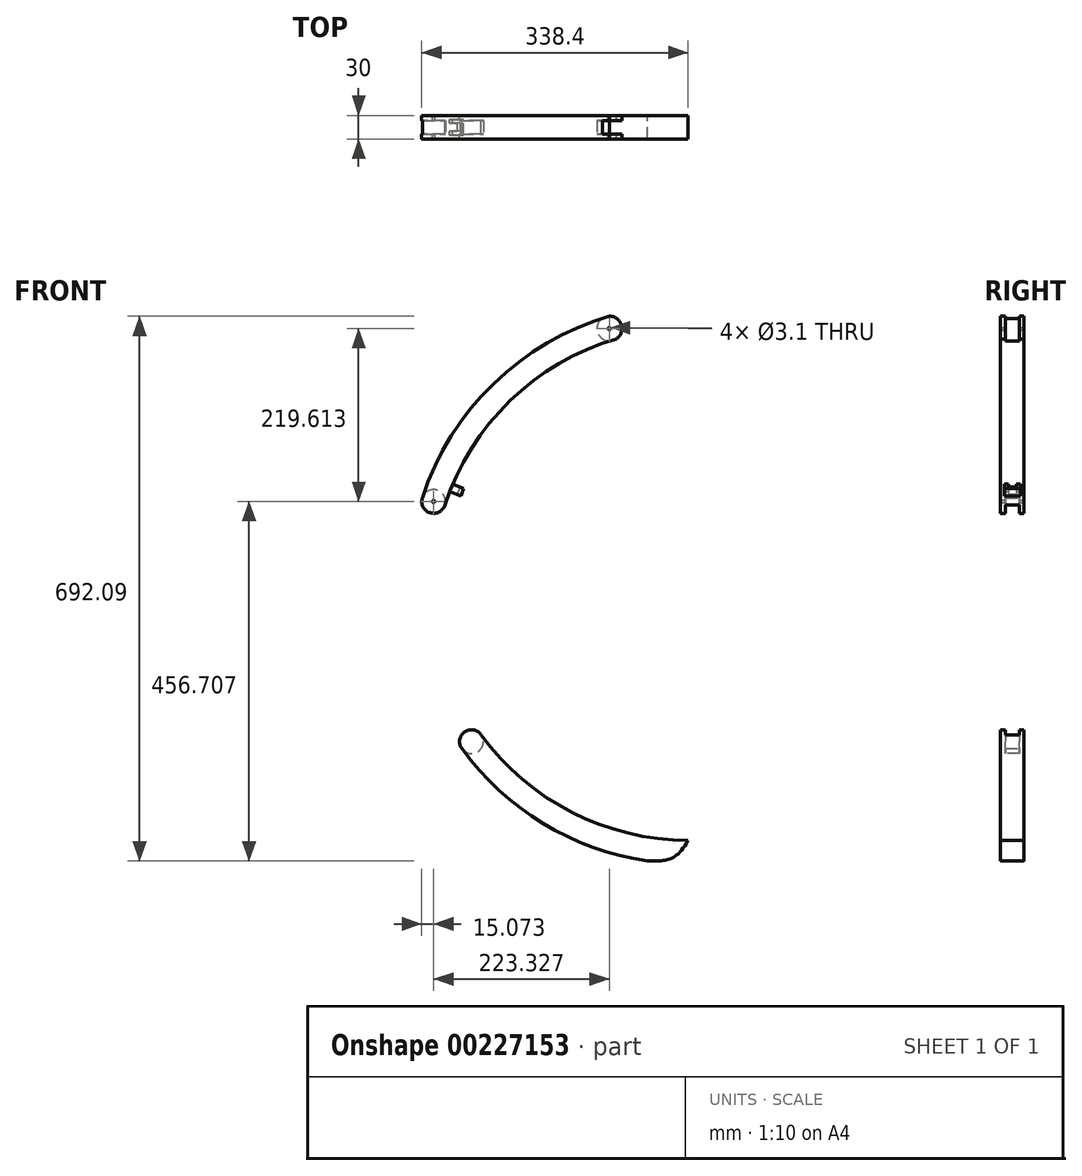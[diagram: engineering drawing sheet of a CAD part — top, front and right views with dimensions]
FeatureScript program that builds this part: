
annotation { "Feature Type Name" : "Feature", "Feature Type Description" : "" }
export const myFeature = defineFeature(function(context is Context, id is Id, definition is map)
    precondition{}
    {
        {
            var Q0;
            Q0=qCreatedBy(makeId("Front.planeOp"),FACE);
            var sketch = newSketch(context, id + "F0", { "sketchPlane" : qUnion([Q0])});
            skLineSegment(sketch, "E0.bottom", {"start": v(-100, 309.23) * mm, "end": v(100, 309.23) * mm});
            skLineSegment(sketch, "E0.top", {"start": v(-100, 340.77) * mm, "end": v(100, 340.77) * mm});
            skLineSegment(sketch, "E0.left", {"start": v(-100, 309.23) * mm, "end": v(-100, 340.77) * mm, "construction": true});
            skLineSegment(sketch, "E0.right", {"start": v(100, 309.23) * mm, "end": v(100, 340.77) * mm});
            skPoint(sketch, "E0.middle", {"position": v(0, 325) * mm});
            skArc(sketch, "E1", {"start": v(-100, 309.23) * mm, "mid": v(-229.54, 230.08) * mm, "end": v(-309, 100.72) * mm});
            skArc(sketch, "E2", {"start": v(-309, 100.72) * mm, "mid": v(-321.03, -50.62) * mm, "end": v(-263.02, -190.9) * mm});
            skArc(sketch, "E3", {"start": v(-263.02, -190.9) * mm, "mid": v(-147.61, -289.54) * mm, "end": v(0, -325) * mm});
            skArc(sketch, "E4", {"start": v(0, -325) * mm, "mid": v(321.03, 50.62) * mm, "end": v(-100, 309.23) * mm});
            skLineSegment(sketch, "E5", {"start": v(0, -325) * mm, "end": v(0, 0) * mm});
            skLineSegment(sketch, "E6", {"start": v(-100, 309.23) * mm, "end": v(-309, 100.72) * mm, "construction": true});
            skLineSegment(sketch, "E7", {"start": v(-263.02, -190.9) * mm, "end": v(-309, 100.72) * mm, "construction": true});
            skLineSegment(sketch, "E8", {"start": v(0, -325) * mm, "end": v(-263.02, -190.9) * mm, "construction": true});
            skCircle(sketch, "E9", {"center": v(-100, 325) * mm, "radius": 15.77 * mm});
            skCircle(sketch, "E10", {"center": v(-100, 325) * mm, "radius": 1.55 * mm});
            skCircle(sketch, "E11", {"center": v(0, 0) * mm, "radius": 355.14 * mm});
            skLineSegment(sketch, "E12", {"start": v(0, 0) * mm, "end": v(-309, 100.72) * mm, "construction": true});
            skLineSegment(sketch, "E13", {"start": v(-309, 100.72) * mm, "end": v(-337.65, 110.06) * mm, "construction": true});
            skCircle(sketch, "E14", {"center": v(-323.33, 105.39) * mm, "radius": 15.07 * mm});
            skCircle(sketch, "E15", {"center": v(-323.33, 105.39) * mm, "radius": 1.55 * mm});
            skLineSegment(sketch, "E16", {"start": v(0, 0) * mm, "end": v(-263.02, -190.9) * mm, "construction": true});
            skLineSegment(sketch, "E17", {"start": v(-263.02, -190.9) * mm, "end": v(-287.4, -208.61) * mm, "construction": true});
            skLineSegment(sketch, "E18", {"start": v(0, -325) * mm, "end": v(0, -355.14) * mm, "construction": true});
            skCircle(sketch, "E19", {"center": v(-275.21, -199.76) * mm, "radius": 15.07 * mm});
            skFitSpline(sketch, "E20", {"points": [v(0, -325) * mm, v(-51.95, -351.32) * mm], "startDerivative": vector(-47.92, -89.33) * mm, "endDerivative": vector(-61.3, -2.04) * mm});
            skLineSegment(sketch, "E21", {"start": v(-330.86, 129.04) * mm, "end": v(0, 0) * mm, "construction": true});
            skLineSegment(sketch, "E22", {"start": v(0, 0) * mm, "end": v(-350.8, -55.31) * mm, "construction": true});
            skLineSegment(sketch, "E23", {"start": v(-302.79, 118.1) * mm, "end": v(-284.01, 110.77) * mm});
            skLineSegment(sketch, "E24", {"start": v(-284.01, 110.77) * mm, "end": v(-280.38, 120.08) * mm});
            skLineSegment(sketch, "E25", {"start": v(-280.38, 120.08) * mm, "end": v(-299, 127.35) * mm});
            skLineSegment(sketch, "E26", {"start": v(-289.7, 123.72) * mm, "end": v(-293.33, 114.4) * mm});
            skLineSegment(sketch, "E27.MirrorCS", {"start": v(-294.73, 77.87) * mm, "end": v(-297.29, 68.2) * mm});
            skLineSegment(sketch, "E28.MirrorCS", {"start": v(-314.22, 83.02) * mm, "end": v(-294.73, 77.87) * mm});
            skLineSegment(sketch, "E29.MirrorCS", {"start": v(-306.96, 70.76) * mm, "end": v(-304.4, 80.43) * mm});
            skLineSegment(sketch, "E30.MirrorCS", {"start": v(-297.29, 68.2) * mm, "end": v(-316.62, 73.31) * mm});
            skLineSegment(sketch, "E31.MirrorCS", {"start": v(-256.47, -164.78) * mm, "end": v(-261.88, -156.37) * mm});
            skLineSegment(sketch, "E32.MirrorCS", {"start": v(-270.3, -161.77) * mm, "end": v(-264.89, -170.19) * mm});
            skLineSegment(sketch, "E33.MirrorCS", {"start": v(-261.88, -156.37) * mm, "end": v(-278.7, -167.18) * mm});
            skLineSegment(sketch, "E34.MirrorCS", {"start": v(-273.43, -175.67) * mm, "end": v(-256.47, -164.78) * mm});
            skLineSegment(sketch, "E35.MirrorCS", {"start": v(-251.76, -205.53) * mm, "end": v(-236.15, -192.78) * mm});
            skLineSegment(sketch, "E36.MirrorCS", {"start": v(-237.57, -206.85) * mm, "end": v(-243.9, -199.1) * mm});
            skLineSegment(sketch, "E37.MirrorCS", {"start": v(-236.15, -192.78) * mm, "end": v(-229.83, -200.53) * mm});
            skLineSegment(sketch, "E38.MirrorCS", {"start": v(-229.83, -200.53) * mm, "end": v(-245.32, -213.18) * mm});
            skLineSegment(sketch, "E39", {"start": v(0, 0) * mm, "end": v(-324.3, 144.75) * mm});
            skLineSegment(sketch, "E40", {"start": v(0, 0) * mm, "end": v(-347.3, 74.16) * mm});
            skLineSegment(sketch, "E41.MirrorCS", {"start": v(0, 0) * mm, "end": v(-307.64, -177.43) * mm});
            skLineSegment(sketch, "E42.MirrorCS", {"start": v(0, 0) * mm, "end": v(-264.03, -237.51) * mm});
            skSolve(sketch);
        }
        {
            var Q0;
            Q0=makeQuery(id+"F0.imprint","IMPRINT",FACE,{"disambiguationData":[TD([[makeQuery(id+"F0.imprint","IMPRINT",EDGE,{"derivedFrom":sQuery(id+"F0.wireOp",EDGE,"E10")}),-1.0]])]});
            var Q1;
            {var subQ3=sQuery(id+"F0.wireOp",EDGE,"E39");var subQ5=sQuery(id+"F0.wireOp",EDGE,"E11");var subQ7=makeQuery(id+"F0.imprint","INTERSECT",VERTEX,{"derivedFrom":[subQ5,subQ3]});Q1=makeQuery(id+"F0.imprint","IMPRINT",FACE,{"disambiguationData":[TD([[makeQuery(id+"F0.imprint","IMPRINT",EDGE,{"disambiguationData":[TD([[subQ7,1.0]])],"derivedFrom":subQ5}),1.0]])]});}
            var Q2;
            {var subQ1=sQuery(id+"F0.wireOp",EDGE,"E1");var subQ8=makeQuery(id+"F0.imprint","INTERSECT",VERTEX,{"derivedFrom":[subQ1,sQuery(id+"F0.wireOp",EDGE,"E25")]});Q2=makeQuery(id+"F0.imprint","IMPRINT",FACE,{"disambiguationData":[TD([[makeQuery(id+"F0.imprint","IMPRINT",EDGE,{"disambiguationData":[TD([[subQ8,1.0]])],"derivedFrom":subQ1}),-1.0]])]});}
            var Q3;
            {var subQ0=sQuery(id+"F0.wireOp",EDGE,"E20");Q3=makeQuery(id+"F0.imprint","IMPRINT",FACE,{"disambiguationData":[TD([[makeQuery(id+"F0.imprint","IMPRINT",EDGE,{"derivedFrom":subQ0}),-1.0]])]});}
            var Q4;
            {var subQ0=sQuery(id+"F0.wireOp",EDGE,"E3");var subQ4=makeQuery(id+"F0.imprint","INTERSECT",VERTEX,{"derivedFrom":[subQ0,sQuery(id+"F0.wireOp",EDGE,"E35.MirrorCS")]});Q4=makeQuery(id+"F0.imprint","IMPRINT",FACE,{"disambiguationData":[TD([[makeQuery(id+"F0.imprint","IMPRINT",EDGE,{"disambiguationData":[TD([[subQ4,-1.0]])],"derivedFrom":subQ0}),-1.0]])]});}
            var Q5;
            Q5=makeQuery(id+"F0.imprint","IMPRINT",FACE,{"disambiguationData":[TD([[makeQuery(id+"F0.imprint","IMPRINT",EDGE,{"derivedFrom":sQuery(id+"F0.wireOp",EDGE,"E15")}),-1.0]])]});
            var Q6;
            {var subQ0=sQuery(id+"F0.wireOp",EDGE,"E19");var subQ2=makeQuery(id+"F0.imprint","INTERSECT",VERTEX,{"derivedFrom":[sQuery(id+"F0.wireOp",EDGE,"E11"),subQ0]});Q6=makeQuery(id+"F0.imprint","IMPRINT",FACE,{"disambiguationData":[TD([[makeQuery(id+"F0.imprint","IMPRINT",EDGE,{"disambiguationData":[TD([[subQ2,1.0]])],"derivedFrom":subQ0}),1.0]])]});}
            var Q7;
            Q7=sQuery(id+"F0.wireOp",EDGE,"E9");
            extrude(context, id + "F1", {"entities" : qUnion([Q0, Q1, Q2, Q3, Q4, Q5, Q6]), "surfaceEntities" : qUnion([Q7]), "endBound" : BoundingType.SYMMETRIC, "depth" : 30 * mm, "offsetDistance" : 25 * mm});
        }
        {
            var Q0;
            {var subQ5=sQuery(id+"F0.wireOp",EDGE,"E26");Q0=makeQuery(id+"F0.imprint","IMPRINT",FACE,{"disambiguationData":[TD([[makeQuery(id+"F0.imprint","IMPRINT",EDGE,{"derivedFrom":subQ5}),-1.0]])]});}
            var Q1;
            {var subQ0=sQuery(id+"F0.wireOp",EDGE,"E24");Q1=makeQuery(id+"F0.imprint","IMPRINT",FACE,{"disambiguationData":[TD([[makeQuery(id+"F0.imprint","IMPRINT",EDGE,{"derivedFrom":subQ0}),1.0]])]});}
            extrude(context, id + "F2", {"entities" : qUnion([Q0, Q1]), "operationType" : NewBodyOperationType.ADD, "endBound" : BoundingType.SYMMETRIC, "depth" : 20 * mm, "offsetDistance" : 25 * mm});
        }
        {
            var Q0;
            {var subQ5=sQuery(id+"F0.wireOp",EDGE,"E26");Q0=makeQuery(id+"F0.imprint","IMPRINT",FACE,{"disambiguationData":[TD([[makeQuery(id+"F0.imprint","IMPRINT",EDGE,{"derivedFrom":subQ5}),-1.0]])]});}
            extrude(context, id + "F3", {"entities" : qUnion([Q0]), "operationType" : NewBodyOperationType.REMOVE, "endBound" : BoundingType.SYMMETRIC, "oppositeDirection" : true, "depth" : 10 * mm, "offsetDistance" : 25 * mm});
        }
        {
            var Q0;
            Q0=makeQuery(id+"F2.opExtrude","SWEPT_FACE",FACE,{"disambiguationData":[OSD([sQuery(id+"F0.wireOp",EDGE,"E24")])]});
            extrude(context, id + "F4", {"entities" : qUnion([Q0]), "operationType" : NewBodyOperationType.REMOVE, "oppositeDirection" : true, "depth" : 5 * mm, "offsetDistance" : 25 * mm});
        }
        {
            var Q0;
            Q0=makeQuery(id+"F0.imprint","IMPRINT",FACE,{"disambiguationData":[TD([[makeQuery(id+"F0.imprint","IMPRINT",EDGE,{"derivedFrom":sQuery(id+"F0.wireOp",EDGE,"E10")}),-1.0]])]});
            var Q1;
            {var subQ0=sQuery(id+"F0.wireOp",EDGE,"E19");var subQ2=makeQuery(id+"F0.imprint","INTERSECT",VERTEX,{"derivedFrom":[sQuery(id+"F0.wireOp",EDGE,"E11"),subQ0]});Q1=makeQuery(id+"F0.imprint","IMPRINT",FACE,{"disambiguationData":[TD([[makeQuery(id+"F0.imprint","IMPRINT",EDGE,{"disambiguationData":[TD([[subQ2,1.0]])],"derivedFrom":subQ0}),1.0]])]});}
            var Q2;
            Q2=makeQuery(id+"F0.imprint","IMPRINT",FACE,{"disambiguationData":[TD([[makeQuery(id+"F0.imprint","IMPRINT",EDGE,{"derivedFrom":sQuery(id+"F0.wireOp",EDGE,"E15")}),-1.0]])]});
            extrude(context, id + "F5", {"entities" : qUnion([Q0, Q1, Q2]), "operationType" : NewBodyOperationType.REMOVE, "endBound" : BoundingType.SYMMETRIC, "oppositeDirection" : true, "depth" : 17.5 * mm, "offsetDistance" : 25 * mm});
        }
    });
